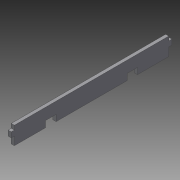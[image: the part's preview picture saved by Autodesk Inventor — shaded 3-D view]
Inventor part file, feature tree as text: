
AUTODESK INVENTOR PART (.ipt)
format: ipt  version: 2015 (Build 190159000, 159)  size: 94,720 bytes
history: native  units: mm
features: extrude x1, sketch x1
ambient origin geometry x8: Origin, YZ Plane, XZ Plane, XY Plane, X Axis, Y Axis, Z Axis, Center Point
bodies: Body1 (feature_tree)
feature tree (2):
  extrude  "Extrusion2"  Depth=5.0mm
  sketch  "Sketch1"  dims[d1=148.0mm d2=5.0mm d3=3.0mm d4=11.0mm d7=10.0mm d9=30.0mm d31=6.0mm d36=3.0mm d37=0.0mm d38=17.0mm d39=8.0mm d40=2.0mm]
